AUTODESK INVENTOR PART (.ipt)
format: ipt  version: 2015 (Build 190159000, 159)  size: 90,112 bytes
history: native  units: mm (DEFAULTED — no unit token found)
features: other x4, plane x3, sketch x1, sweep x1
ambient origin geometry x8: Origin, YZ Plane, XZ Plane, XY Plane, X Axis, Y Axis, Z Axis, Center Point
bodies: Solid1 (feature_tree)
feature tree (9):
  sketch  "草图路径"  dims[d0=19.05mm d2=0.0mm d4=0.6858mm d5=1.3462mm d6=0.0mm d7=0.0mm d8=0.0mm d9=0.0mm d10=0.0mm d11=0.0mm d12=0.0mm d13=0.0mm]
  other  "截面平面"
  other  "工作轴1"
  other  "工作轴2"
  other  "工作轴3"
  plane  "工作平面2"
  plane  "工作平面3"
  plane  "工作平面4"
  sweep  "皮带"
